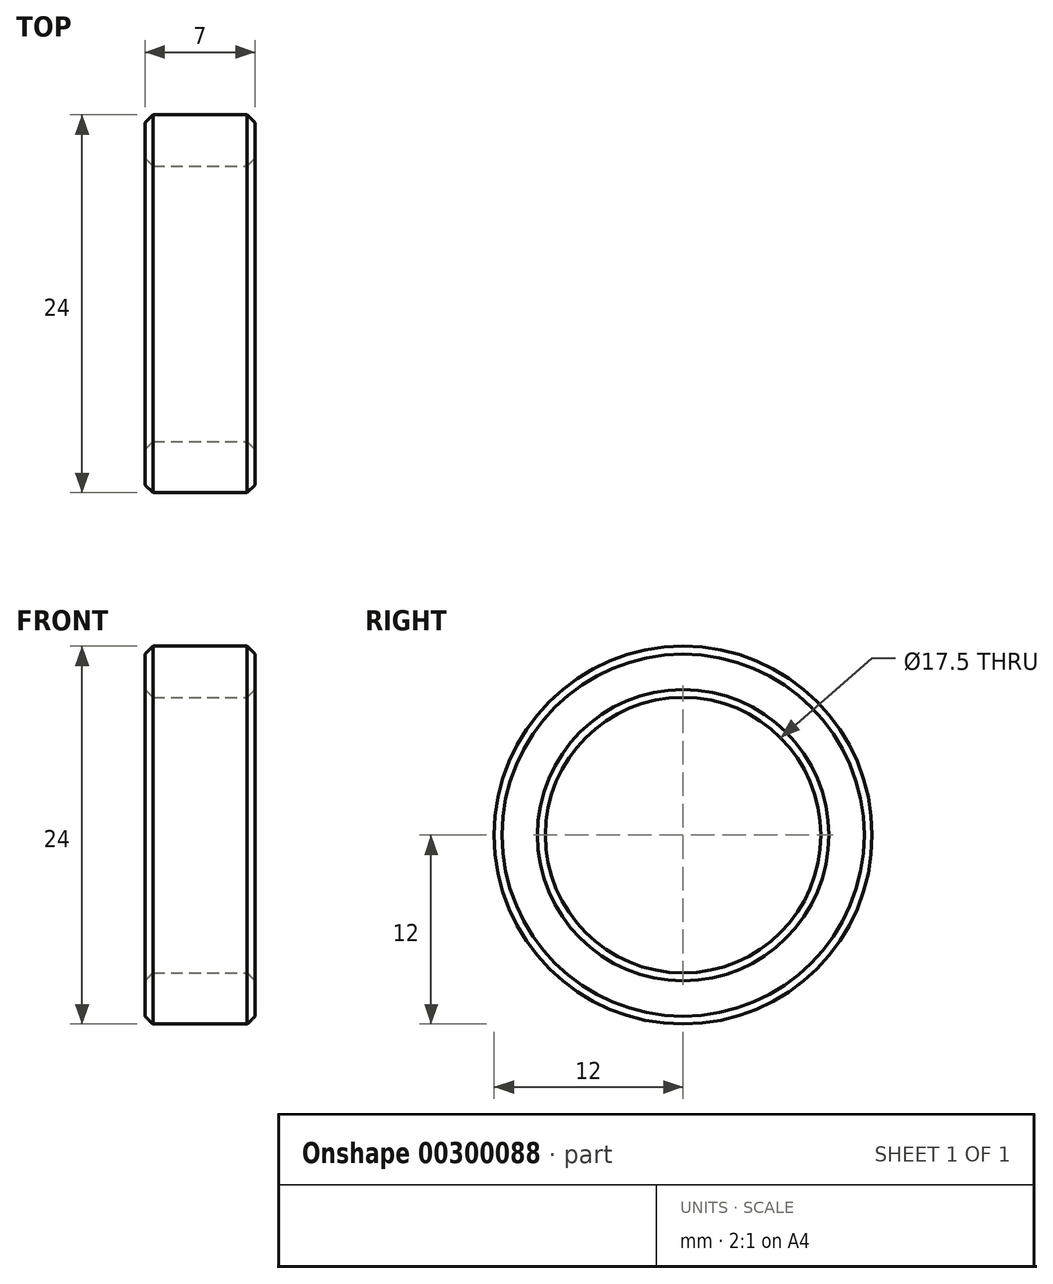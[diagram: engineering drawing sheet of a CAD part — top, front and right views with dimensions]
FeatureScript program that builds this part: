
annotation { "Feature Type Name" : "Feature", "Feature Type Description" : "" }
export const myFeature = defineFeature(function(context is Context, id is Id, definition is map)
    precondition{}
    {
        {
            var Q0;
            Q0=qCreatedBy(makeId("Front.planeOp"),FACE);
            var sketch = newSketch(context, id + "F0", { "sketchPlane" : qUnion([Q0])});
            skLineSegment(sketch, "E0.bottom", {"start": v(0, 8.75) * mm, "end": v(-7, 8.75) * mm});
            skLineSegment(sketch, "E0.top", {"start": v(0, 12) * mm, "end": v(-7, 12) * mm});
            skLineSegment(sketch, "E0.left", {"start": v(0, 8.75) * mm, "end": v(0, 12) * mm});
            skLineSegment(sketch, "E0.right", {"start": v(-7, 8.75) * mm, "end": v(-7, 12) * mm});
            skLineSegment(sketch, "E1", {"start": v(0, 0) * mm, "end": v(-20.38, 0) * mm, "construction": true});
            skSolve(sketch);
        }
        {
            var Q0;
            Q0=makeQuery(id+"F0.imprint","IMPRINT",FACE,{"disambiguationData":[TD([[makeQuery(id+"F0.imprint","IMPRINT",EDGE,{"derivedFrom":sQuery(id+"F0.wireOp",EDGE,"E0.bottom")}),-1.0]])]});
            var Q1;
            Q1=sQuery(id+"F0.wireOp",EDGE,"E1");
            revolve(context, id + "F1", {"entities" : qUnion([Q0]), "axis" : qUnion([Q1]), "revolveType" : RevolveType.FULL});
        }
        {
            var Q0;
            Q0=makeQuery(id+"F1.opRevolve","SWEPT_EDGE",EDGE,{"disambiguationData":[OSD([sQuery(id+"F0.wireOp",EDGE,"E0.top"),sQuery(id+"F0.wireOp",EDGE,"E0.left")])]});
            var Q1;
            Q1=makeQuery(id+"F1.opRevolve","SWEPT_EDGE",EDGE,{"disambiguationData":[OSD([sQuery(id+"F0.wireOp",EDGE,"E0.bottom"),sQuery(id+"F0.wireOp",EDGE,"E0.left")])]});
            var Q2;
            Q2=makeQuery(id+"F1.opRevolve","SWEPT_EDGE",EDGE,{"disambiguationData":[OSD([sQuery(id+"F0.wireOp",EDGE,"E0.top"),sQuery(id+"F0.wireOp",EDGE,"E0.right")])]});
            var Q3;
            Q3=makeQuery(id+"F1.opRevolve","SWEPT_EDGE",EDGE,{"disambiguationData":[OSD([sQuery(id+"F0.wireOp",EDGE,"E0.bottom"),sQuery(id+"F0.wireOp",EDGE,"E0.right")])]});
            chamfer(context, id + "F2", {"entities" : qUnion([Q0, Q1, Q2, Q3]), "width" : 0.5 * mm, "tangentPropagation" : true});
        }
    });
